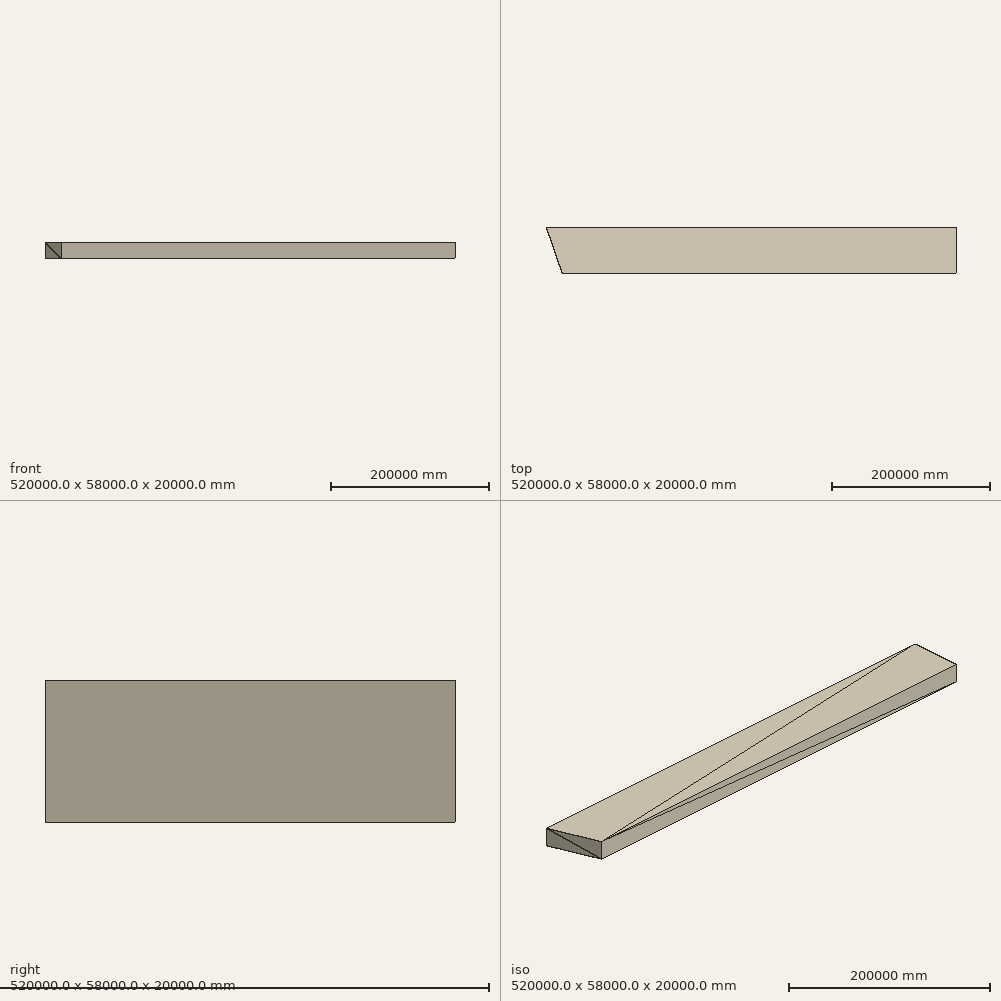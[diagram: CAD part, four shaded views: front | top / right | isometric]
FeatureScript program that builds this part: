
annotation { "Feature Type Name" : "Feature", "Feature Type Description" : "" }
export const myFeature = defineFeature(function(context is Context, id is Id, definition is map)
    precondition{}
    {
        {
            var Q0;
            Q0=qCreatedBy(makeId("Top.planeOp"),FACE);
            var sketch = newSketch(context, id + "F0", { "sketchPlane" : qUnion([Q0])});
            skLineSegment(sketch, "E0", {"start": v(-320000, 0) * mm, "end": v(200000, 0) * mm});
            skLineSegment(sketch, "E1", {"start": v(200000, 0) * mm, "end": v(200000, -58000) * mm});
            skLineSegment(sketch, "E2", {"start": v(200000, -58000) * mm, "end": v(-300000, -58000) * mm});
            skLineSegment(sketch, "E3", {"start": v(-300000, -58000) * mm, "end": v(-320000, 0) * mm});
            skSolve(sketch);
        }
        {
            var Q0;
            Q0 = qSketchRegion(id + "F0", true);
            extrude(context, id + "F1", {"entities" : qUnion([Q0]), "oppositeDirection" : true, "depth" : 20000 * mm, "offsetDistance" : 25 * mm});
        }
    });
